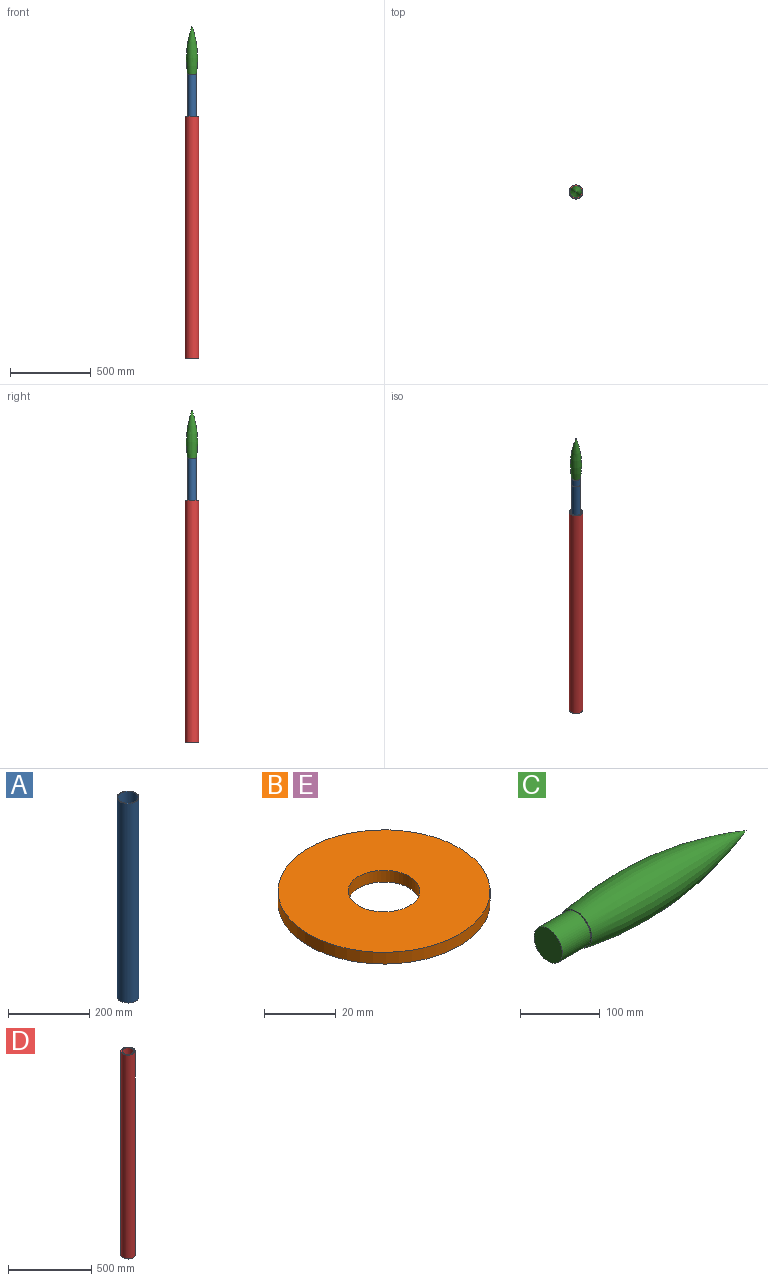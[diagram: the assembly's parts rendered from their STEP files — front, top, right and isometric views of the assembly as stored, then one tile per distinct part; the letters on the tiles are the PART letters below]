
ASSEMBLY  parts=5 mates=4
PART A: 4 faces, bbox 54x54x600 mm
  f0: cylinder r=25mm len=600mm, axis (0,0,-1), area 94247.8mm2, adj f2,f3
  f1: cylinder r=27mm len=600mm, axis (0,0,-1), area 101787.6mm2, adj f2,f3
  f2: plane 54x54mm, normal (0,0,1), area 326.7mm2, adj f0,f1
  f3: plane 54x54mm, normal (0,0,-1), area 326.7mm2, adj f0,f1
PART B: 4 faces, bbox 59x59x4 mm
  f0: cylinder r=10mm len=20mm, axis (0,0,-1), area 251.3mm2, adj f2,f3
  f1: cylinder r=29.5mm len=59mm, axis (0,0,-1), area 741.4mm2, adj f2,f3
  f2: plane 59x59mm, normal (0,0,1), area 2419.8mm2, adj f0,f1
  f3: plane 59x59mm, normal (0,0,-1), area 2419.8mm2, adj f0,f1
PART C: 4 faces, bbox 350x70.1x70.1 mm
  f0: cylinder r=25mm len=50mm, axis (-1,0,0), area 7854mm2, adj f1,f3
  f1: plane 50x50mm, normal (-1,0,0), area 1963.5mm2, adj f0
  f2: revolved ~300x70.08mm, area 50199.9mm2, adj f3
  f3: plane 54x54mm, normal (-1,0,0), area 326.7mm2, adj f0,f2
PART D: 4 faces, bbox 85x85x1500 mm
  f0: cylinder r=35mm len=1500mm, axis (0,0,-1), area 329867.2mm2, adj f2,f3
  f1: cylinder r=42.5mm len=1500mm, axis (0,0,-1), area 400553.1mm2, adj f2,f3
  f2: plane 85x85mm, normal (0,0,1), area 1826.1mm2, adj f0,f1
  f3: plane 85x85mm, normal (0,0,-1), area 1826.1mm2, adj f0,f1
PART E: same geometry as B
PLACE A at identity fixed
PLACE B t=(0,0,50)mm
PLACE C rot(axis=(0.71,0,0.71),180deg) t=(0,0,550)mm
PLACE D t=(0,0,-1158)mm
PLACE E at identity
MATE fastened C.f0 <-> A.f0  axis (0,0,-1) through (0,0,600)mm
MATE fastened B.f1 <-> A.f1  axis (0,0,-1) through (0,0,50)mm
MATE fastened E.f1 <-> A.f1  axis (0,0,-1) through (0,0,0)mm
MATE slider D.f1 <-> A.f1  axis (0,0,-1) through (0,0,-408)mm
